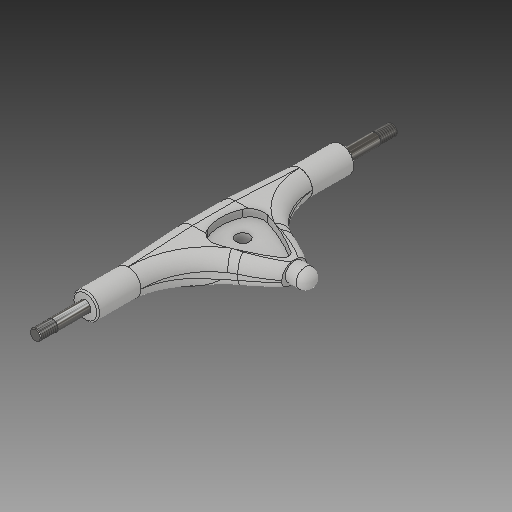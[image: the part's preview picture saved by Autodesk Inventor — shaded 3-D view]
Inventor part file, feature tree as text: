
AUTODESK INVENTOR PART (.ipt)
format: ipt  version: 2019 (Build 230136000, 136)  size: 438,272 bytes
history: native  units: mm
features: extrude x12, sketch x11, chamfer x7, fillet x5, other x3, thread x2
ambient origin geometry x8: Origin, YZ Plane, XZ Plane, XY Plane, X Axis, Y Axis, Z Axis, Center Point
bodies: Body1 (feature_tree)
feature tree (40):
  other  "Твердое тело1"
  sketch  "Эскиз1"
  extrude  "Выдавливание1"  Depth=18.0mm
  extrude  "Выдавливание2"  Depth=180.0mm TaperAngle=0.0deg
  chamfer  "Фаска1"  Distance=23.0mm
  chamfer  "Фаска2"  Distance=30.0mm
  sketch  "Эскиз2"
  extrude  "Выдавливание3"  Depth=45.0mm TaperAngle=45.0deg
  extrude  "Выдавливание4"  Depth=45.0mm TaperAngle=45.0deg
  extrude  "Выдавливание5"  Depth=8.0mm
  extrude  "Выдавливание6"  Depth=35.0mm TaperAngle=0.0deg
  chamfer  "Фаска3"  Distance=35.0mm
  fillet  "Сопряжение1"  Radius=0.1mm
  sketch  "Эскиз6"
  other  "РабПлоскость3"
  extrude  "Выдавливание10"  Depth=12.0mm TaperAngle=0.0deg
  chamfer  "Фаска4"  Distance=12.0mm
  chamfer  "Фаска5"  Distance=0.5mm Angle=45.0deg
  chamfer  "Фаска6"  Distance=1.0mm
  chamfer  "Фаска7"  Distance=68.0mm
  extrude  "Выдавливание12"  Depth=140.0mm
  fillet  "Сопряжение7"  Radius=108.0mm
  fillet  "Сопряжение8"  Radius=18.0mm
  extrude  "Выдавливание13"  Depth=23.0mm TaperAngle=0.0deg
  fillet  "Сопряжение9"  Radius=45.0mm
  extrude  "Выдавливание14"  Depth=45.0mm TaperAngle=45.0deg
  fillet  "Сопряжение11"  Radius=45.0mm
  extrude  "Выдавливание15"  Depth=45.0mm TaperAngle=45.0deg
  thread  "Резьба1"
  thread  "Резьба2"
  other  "РабПлоскость4"
  extrude  "Выдавливание16"  Depth=14.0mm
  sketch  "Эскиз3"
  sketch  "Эскиз4"
  sketch  "Эскиз5"
  sketch  "Эскиз22"
  sketch  "Эскиз23"
  sketch  "Эскиз24"
  sketch  "Эскиз25"
  sketch  "Эскиз26"
